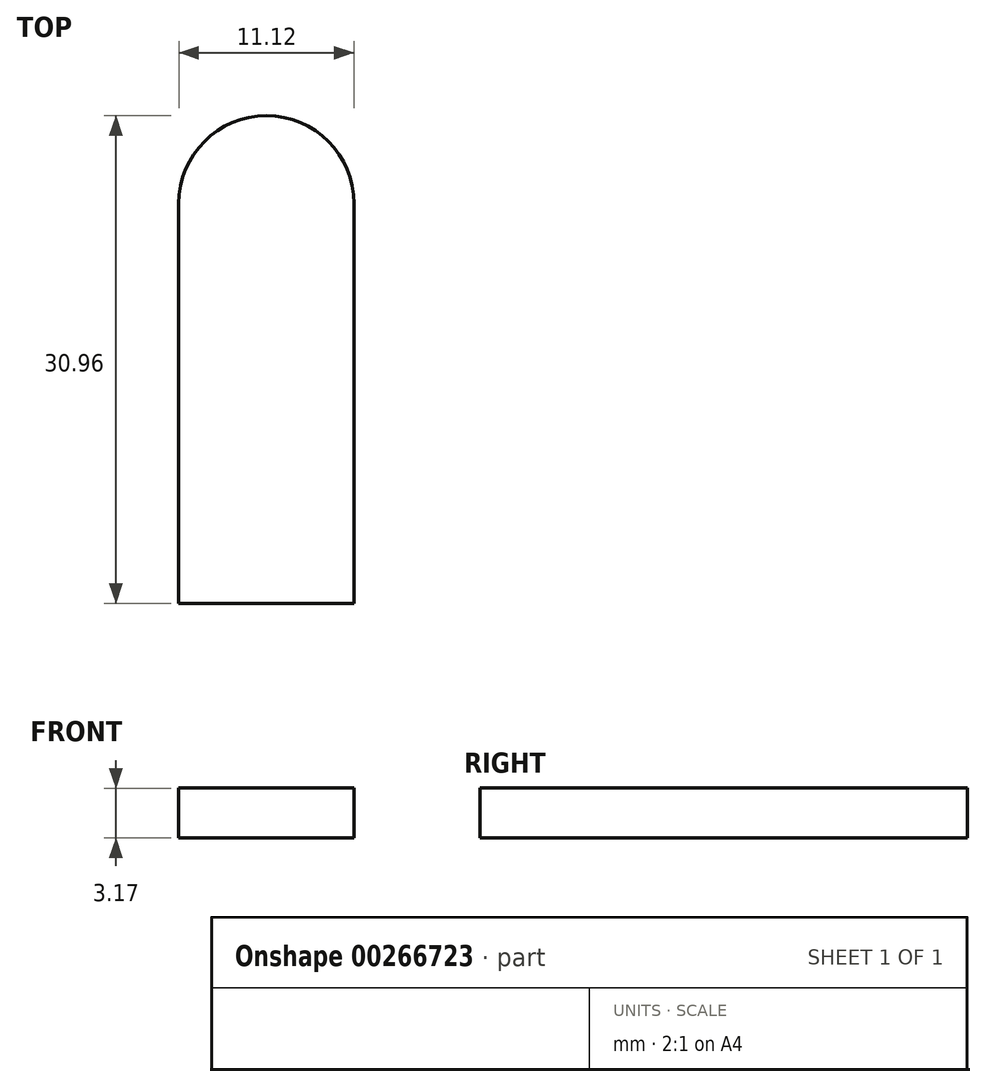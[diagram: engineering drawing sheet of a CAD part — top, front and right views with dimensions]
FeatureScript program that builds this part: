
annotation { "Feature Type Name" : "Feature", "Feature Type Description" : "" }
export const myFeature = defineFeature(function(context is Context, id is Id, definition is map)
    precondition{}
    {
        {
            var Q0;
            Q0=qCreatedBy(makeId("Top.planeOp"),FACE);
            var sketch = newSketch(context, id + "F0", { "sketchPlane" : qUnion([Q0])});
            skArc(sketch, "E0", {"start": v(5.56, 0) * mm, "mid": v(0, 5.56) * mm, "end": v(-5.56, 0) * mm});
            skLineSegment(sketch, "E1", {"start": v(-5.56, 0) * mm, "end": v(-5.56, -25.4) * mm});
            skLineSegment(sketch, "E2", {"start": v(5.56, 0) * mm, "end": v(5.56, -25.4) * mm});
            skLineSegment(sketch, "E3", {"start": v(-5.56, -25.4) * mm, "end": v(5.56, -25.4) * mm});
            skSolve(sketch);
        }
        {
            var Q0;
            Q0=makeQuery(id+"F0.imprint","IMPRINT",FACE,{"disambiguationData":[TD([[makeQuery(id+"F0.imprint","IMPRINT",EDGE,{"derivedFrom":sQuery(id+"F0.wireOp",EDGE,"E0")}),1.0]])]});
            extrude(context, id + "F1", {"entities" : qUnion([Q0]), "depth" : 3.17 * mm});
        }
    });
